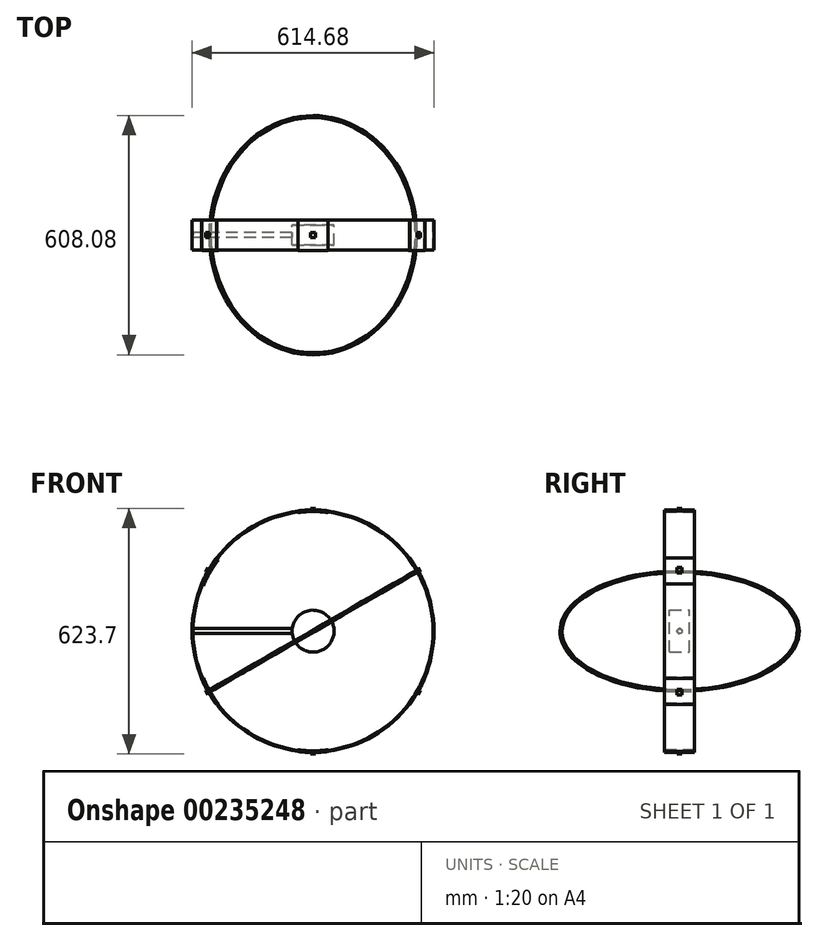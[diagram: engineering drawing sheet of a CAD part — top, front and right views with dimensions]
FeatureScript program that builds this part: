
annotation { "Feature Type Name" : "Feature", "Feature Type Description" : "" }
export const myFeature = defineFeature(function(context is Context, id is Id, definition is map)
    precondition{}
    {
        {
            var Q0;
            Q0=qCreatedBy(makeId("Front.planeOp"),FACE);
            var sketch = newSketch(context, id + "F0", { "sketchPlane" : qUnion([Q0])});
            skCircle(sketch, "E0", {"center": v(0, 0) * mm, "radius": 304.8 * mm});
            skCircle(sketch, "E1.0", {"center": v(0, 0) * mm, "radius": 307.34 * mm});
            skSolve(sketch);
        }
        {
            var Q0;
            Q0 = qSketchRegion(id + "F0", true);
            extrude(context, id + "F1", {"entities" : qUnion([Q0]), "endBound" : BoundingType.SYMMETRIC, "depth" : 76.2 * mm});
        }
        {
            var Q0;
            Q0=makeQuery(id+"F1.opExtrude","CAP_FACE",FACE,{"disambiguationData":[OSD([sQuery(id+"F0.wireOp",EDGE,"E0"),sQuery(id+"F0.wireOp",EDGE,"E1.0")])],"isStart":false});
            var sketch = newSketch(context, id + "F2", { "sketchPlane" : qUnion([Q0])});
            skLineSegment(sketch, "E2", {"start": v(0, 304.8) * mm, "end": v(0, 287.98) * mm, "construction": true});
            skArc(sketch, "E3.0", {"start": v(38.1, 304.97) * mm, "mid": v(0, 307.34) * mm, "end": v(-38.1, 304.97) * mm});
            skArc(sketch, "E4.0", {"start": v(38.1, 302.4) * mm, "mid": v(0, 304.8) * mm, "end": v(-38.1, 302.4) * mm});
            skLineSegment(sketch, "E5", {"start": v(-38.1, 302.4) * mm, "end": v(-38.1, 304.97) * mm, "construction": true});
            skLineSegment(sketch, "E6", {"start": v(38.1, 304.97) * mm, "end": v(38.1, 302.4) * mm, "construction": true});
            skArc(sketch, "E7.0", {"start": v(38.1, 301.64) * mm, "mid": v(0, 304.04) * mm, "end": v(-38.1, 301.64) * mm});
            skArc(sketch, "E8.0", {"start": v(38.1, 305.74) * mm, "mid": v(0, 308.1) * mm, "end": v(-38.1, 305.74) * mm});
            skLineSegment(sketch, "E9", {"start": v(-38.1, 302.4) * mm, "end": v(-38.1, 301.64) * mm});
            skLineSegment(sketch, "E10", {"start": v(-38.1, 304.97) * mm, "end": v(-38.1, 305.74) * mm});
            skLineSegment(sketch, "E11", {"start": v(38.1, 302.4) * mm, "end": v(38.1, 301.64) * mm});
            skLineSegment(sketch, "E12", {"start": v(38.1, 304.97) * mm, "end": v(38.1, 305.74) * mm});
            skArc(sketch, "E13.1.0", {"start": v(280.94, 118.2) * mm, "mid": v(263.96, 152.4) * mm, "end": v(242.84, 184.2) * mm});
            skArc(sketch, "E13.1.1", {"start": v(280.28, 117.83) * mm, "mid": v(263.3, 152.02) * mm, "end": v(242.18, 183.82) * mm});
            skArc(sketch, "E13.1.2", {"start": v(283.83, 119.87) * mm, "mid": v(266.82, 154.05) * mm, "end": v(245.73, 185.86) * mm});
            skArc(sketch, "E13.1.3", {"start": v(283.16, 119.49) * mm, "mid": v(266.16, 153.67) * mm, "end": v(245.06, 185.48) * mm});
            skLineSegment(sketch, "E13.1.4", {"start": v(242.84, 184.2) * mm, "end": v(245.06, 185.48) * mm, "construction": true});
            skLineSegment(sketch, "E13.1.5", {"start": v(283.16, 119.49) * mm, "end": v(280.94, 118.2) * mm, "construction": true});
            skLineSegment(sketch, "E13.1.6", {"start": v(242.84, 184.2) * mm, "end": v(242.18, 183.82) * mm});
            skLineSegment(sketch, "E13.1.7", {"start": v(245.06, 185.48) * mm, "end": v(245.73, 185.86) * mm});
            skLineSegment(sketch, "E13.1.8", {"start": v(280.94, 118.2) * mm, "end": v(280.28, 117.83) * mm});
            skLineSegment(sketch, "E13.1.9", {"start": v(283.16, 119.49) * mm, "end": v(283.83, 119.87) * mm});
            skArc(sketch, "E13.2.0", {"start": v(242.84, -184.2) * mm, "mid": v(263.96, -152.4) * mm, "end": v(280.94, -118.2) * mm});
            skArc(sketch, "E13.2.1", {"start": v(242.18, -183.82) * mm, "mid": v(263.3, -152.02) * mm, "end": v(280.28, -117.83) * mm});
            skArc(sketch, "E13.2.2", {"start": v(245.73, -185.86) * mm, "mid": v(266.82, -154.05) * mm, "end": v(283.83, -119.87) * mm});
            skArc(sketch, "E13.2.3", {"start": v(245.06, -185.48) * mm, "mid": v(266.16, -153.67) * mm, "end": v(283.16, -119.49) * mm});
            skLineSegment(sketch, "E13.2.4", {"start": v(280.94, -118.2) * mm, "end": v(283.16, -119.49) * mm, "construction": true});
            skLineSegment(sketch, "E13.2.5", {"start": v(245.06, -185.48) * mm, "end": v(242.84, -184.2) * mm, "construction": true});
            skLineSegment(sketch, "E13.2.6", {"start": v(280.94, -118.2) * mm, "end": v(280.28, -117.83) * mm});
            skLineSegment(sketch, "E13.2.7", {"start": v(283.16, -119.49) * mm, "end": v(283.83, -119.87) * mm});
            skLineSegment(sketch, "E13.2.8", {"start": v(242.84, -184.2) * mm, "end": v(242.18, -183.82) * mm});
            skLineSegment(sketch, "E13.2.9", {"start": v(245.06, -185.48) * mm, "end": v(245.73, -185.86) * mm});
            skArc(sketch, "E13.3.0", {"start": v(-38.1, -302.4) * mm, "mid": v(0, -304.8) * mm, "end": v(38.1, -302.4) * mm});
            skArc(sketch, "E13.3.1", {"start": v(-38.1, -301.64) * mm, "mid": v(0, -304.04) * mm, "end": v(38.1, -301.64) * mm});
            skArc(sketch, "E13.3.2", {"start": v(-38.1, -305.74) * mm, "mid": v(0, -308.1) * mm, "end": v(38.1, -305.74) * mm});
            skArc(sketch, "E13.3.3", {"start": v(-38.1, -304.97) * mm, "mid": v(0, -307.34) * mm, "end": v(38.1, -304.97) * mm});
            skLineSegment(sketch, "E13.3.4", {"start": v(38.1, -302.4) * mm, "end": v(38.1, -304.97) * mm, "construction": true});
            skLineSegment(sketch, "E13.3.5", {"start": v(-38.1, -304.97) * mm, "end": v(-38.1, -302.4) * mm, "construction": true});
            skLineSegment(sketch, "E13.3.6", {"start": v(38.1, -302.4) * mm, "end": v(38.1, -301.64) * mm});
            skLineSegment(sketch, "E13.3.7", {"start": v(38.1, -304.97) * mm, "end": v(38.1, -305.74) * mm});
            skLineSegment(sketch, "E13.3.8", {"start": v(-38.1, -302.4) * mm, "end": v(-38.1, -301.64) * mm});
            skLineSegment(sketch, "E13.3.9", {"start": v(-38.1, -304.97) * mm, "end": v(-38.1, -305.74) * mm});
            skArc(sketch, "E13.4.0", {"start": v(-280.94, -118.2) * mm, "mid": v(-263.96, -152.4) * mm, "end": v(-242.84, -184.2) * mm});
            skArc(sketch, "E13.4.1", {"start": v(-280.28, -117.83) * mm, "mid": v(-263.3, -152.02) * mm, "end": v(-242.18, -183.82) * mm});
            skArc(sketch, "E13.4.2", {"start": v(-283.83, -119.87) * mm, "mid": v(-266.82, -154.05) * mm, "end": v(-245.73, -185.86) * mm});
            skArc(sketch, "E13.4.3", {"start": v(-283.16, -119.49) * mm, "mid": v(-266.16, -153.67) * mm, "end": v(-245.06, -185.48) * mm});
            skLineSegment(sketch, "E13.4.4", {"start": v(-242.84, -184.2) * mm, "end": v(-245.06, -185.48) * mm, "construction": true});
            skLineSegment(sketch, "E13.4.5", {"start": v(-283.16, -119.49) * mm, "end": v(-280.94, -118.2) * mm, "construction": true});
            skLineSegment(sketch, "E13.4.6", {"start": v(-242.84, -184.2) * mm, "end": v(-242.18, -183.82) * mm});
            skLineSegment(sketch, "E13.4.7", {"start": v(-245.06, -185.48) * mm, "end": v(-245.73, -185.86) * mm});
            skLineSegment(sketch, "E13.4.8", {"start": v(-280.94, -118.2) * mm, "end": v(-280.28, -117.83) * mm});
            skLineSegment(sketch, "E13.4.9", {"start": v(-283.16, -119.49) * mm, "end": v(-283.83, -119.87) * mm});
            skArc(sketch, "E13.5.0", {"start": v(-242.84, 184.2) * mm, "mid": v(-263.96, 152.4) * mm, "end": v(-280.94, 118.2) * mm});
            skArc(sketch, "E13.5.1", {"start": v(-242.18, 183.82) * mm, "mid": v(-263.3, 152.02) * mm, "end": v(-280.28, 117.83) * mm});
            skArc(sketch, "E13.5.2", {"start": v(-245.73, 185.86) * mm, "mid": v(-266.82, 154.05) * mm, "end": v(-283.83, 119.87) * mm});
            skArc(sketch, "E13.5.3", {"start": v(-245.06, 185.48) * mm, "mid": v(-266.16, 153.67) * mm, "end": v(-283.16, 119.49) * mm});
            skLineSegment(sketch, "E13.5.4", {"start": v(-280.94, 118.2) * mm, "end": v(-283.16, 119.49) * mm, "construction": true});
            skLineSegment(sketch, "E13.5.5", {"start": v(-245.06, 185.48) * mm, "end": v(-242.84, 184.2) * mm, "construction": true});
            skLineSegment(sketch, "E13.5.6", {"start": v(-280.94, 118.2) * mm, "end": v(-280.28, 117.83) * mm});
            skLineSegment(sketch, "E13.5.7", {"start": v(-283.16, 119.49) * mm, "end": v(-283.83, 119.87) * mm});
            skLineSegment(sketch, "E13.5.8", {"start": v(-242.84, 184.2) * mm, "end": v(-242.18, 183.82) * mm});
            skLineSegment(sketch, "E13.5.9", {"start": v(-245.06, 185.48) * mm, "end": v(-245.73, 185.86) * mm});
            skLineSegment(sketch, "E13.anchor1", {"start": v(0, 0) * mm, "end": v(-38.1, 301.64) * mm, "construction": true});
            skLineSegment(sketch, "E13.anchor2", {"start": v(0, 0) * mm, "end": v(-38.1, 301.64) * mm, "construction": true});
            skSolve(sketch);
        }
        {
            var Q0;
            Q0 = qSketchRegion(id + "F2", true);
            var Q1;
            Q1=makeQuery(id+"F1.opExtrude","CAP_FACE",FACE,{"disambiguationData":[OSD([sQuery(id+"F0.wireOp",EDGE,"E0"),sQuery(id+"F0.wireOp",EDGE,"E1.0")])],"isStart":true});
            extrude(context, id + "F3", {"entities" : qUnion([Q0]), "operationType" : NewBodyOperationType.ADD, "endBound" : BoundingType.UP_TO_SURFACE, "oppositeDirection" : true, "endBoundEntityFace" : qUnion([Q1]), "depth" : 162.56 * mm});
        }
        {
            var Q0;
            Q0=makeQuery(id+"F3.boolean.opBoolean","MERGE",FACE,{"derivedFrom":[makeQuery(id+"F1.opExtrude","CAP_FACE",FACE,{"disambiguationData":[OSD([sQuery(id+"F0.wireOp",EDGE,"E0"),sQuery(id+"F0.wireOp",EDGE,"E1.0")])],"isStart":false}),makeQuery(id+"F3.opExtrude","CAP_FACE",FACE,{"disambiguationData":[OSD([sQuery(id+"F2.wireOp",EDGE,"E13.1.0"),sQuery(id+"F2.wireOp",EDGE,"E13.1.1"),sQuery(id+"F2.wireOp",EDGE,"E13.1.6"),sQuery(id+"F2.wireOp",EDGE,"E13.1.8")])],"isStart":true}),makeQuery(id+"F3.opExtrude","CAP_FACE",FACE,{"disambiguationData":[OSD([sQuery(id+"F2.wireOp",EDGE,"E13.1.2"),sQuery(id+"F2.wireOp",EDGE,"E13.1.3"),sQuery(id+"F2.wireOp",EDGE,"E13.1.7"),sQuery(id+"F2.wireOp",EDGE,"E13.1.9")])],"isStart":true}),makeQuery(id+"F3.opExtrude","CAP_FACE",FACE,{"disambiguationData":[OSD([sQuery(id+"F2.wireOp",EDGE,"E13.2.0"),sQuery(id+"F2.wireOp",EDGE,"E13.2.1"),sQuery(id+"F2.wireOp",EDGE,"E13.2.6"),sQuery(id+"F2.wireOp",EDGE,"E13.2.8")])],"isStart":true}),makeQuery(id+"F3.opExtrude","CAP_FACE",FACE,{"disambiguationData":[OSD([sQuery(id+"F2.wireOp",EDGE,"E13.2.2"),sQuery(id+"F2.wireOp",EDGE,"E13.2.3"),sQuery(id+"F2.wireOp",EDGE,"E13.2.7"),sQuery(id+"F2.wireOp",EDGE,"E13.2.9")])],"isStart":true}),makeQuery(id+"F3.opExtrude","CAP_FACE",FACE,{"disambiguationData":[OSD([sQuery(id+"F2.wireOp",EDGE,"E13.3.0"),sQuery(id+"F2.wireOp",EDGE,"E13.3.1"),sQuery(id+"F2.wireOp",EDGE,"E13.3.6"),sQuery(id+"F2.wireOp",EDGE,"E13.3.8")])],"isStart":true}),makeQuery(id+"F3.opExtrude","CAP_FACE",FACE,{"disambiguationData":[OSD([sQuery(id+"F2.wireOp",EDGE,"E13.3.2"),sQuery(id+"F2.wireOp",EDGE,"E13.3.3"),sQuery(id+"F2.wireOp",EDGE,"E13.3.7"),sQuery(id+"F2.wireOp",EDGE,"E13.3.9")])],"isStart":true}),makeQuery(id+"F3.opExtrude","CAP_FACE",FACE,{"disambiguationData":[OSD([sQuery(id+"F2.wireOp",EDGE,"E13.4.0"),sQuery(id+"F2.wireOp",EDGE,"E13.4.1"),sQuery(id+"F2.wireOp",EDGE,"E13.4.6"),sQuery(id+"F2.wireOp",EDGE,"E13.4.8")])],"isStart":true}),makeQuery(id+"F3.opExtrude","CAP_FACE",FACE,{"disambiguationData":[OSD([sQuery(id+"F2.wireOp",EDGE,"E13.4.2"),sQuery(id+"F2.wireOp",EDGE,"E13.4.3"),sQuery(id+"F2.wireOp",EDGE,"E13.4.7"),sQuery(id+"F2.wireOp",EDGE,"E13.4.9")])],"isStart":true}),makeQuery(id+"F3.opExtrude","CAP_FACE",FACE,{"disambiguationData":[OSD([sQuery(id+"F2.wireOp",EDGE,"E13.5.0"),sQuery(id+"F2.wireOp",EDGE,"E13.5.1"),sQuery(id+"F2.wireOp",EDGE,"E13.5.6"),sQuery(id+"F2.wireOp",EDGE,"E13.5.8")])],"isStart":true}),makeQuery(id+"F3.opExtrude","CAP_FACE",FACE,{"disambiguationData":[OSD([sQuery(id+"F2.wireOp",EDGE,"E13.5.2"),sQuery(id+"F2.wireOp",EDGE,"E13.5.3"),sQuery(id+"F2.wireOp",EDGE,"E13.5.7"),sQuery(id+"F2.wireOp",EDGE,"E13.5.9")])],"isStart":true}),makeQuery(id+"F3.opExtrude","CAP_FACE",FACE,{"disambiguationData":[OSD([sQuery(id+"F2.wireOp",EDGE,"E4.0"),sQuery(id+"F2.wireOp",EDGE,"E7.0"),sQuery(id+"F2.wireOp",EDGE,"E9"),sQuery(id+"F2.wireOp",EDGE,"E11")])],"isStart":true}),makeQuery(id+"F3.opExtrude","CAP_FACE",FACE,{"disambiguationData":[OSD([sQuery(id+"F2.wireOp",EDGE,"E8.0"),sQuery(id+"F2.wireOp",EDGE,"E3.0"),sQuery(id+"F2.wireOp",EDGE,"E10"),sQuery(id+"F2.wireOp",EDGE,"E12")])],"isStart":true})]});
            var sketch = newSketch(context, id + "F4", { "sketchPlane" : qUnion([Q0])});
            skArc(sketch, "E14.0", {"start": v(38.1, 305.74) * mm, "mid": v(0, 308.1) * mm, "end": v(-38.1, 305.74) * mm});
            skArc(sketch, "E14.1", {"start": v(38.1, 301.64) * mm, "mid": v(0, 304.04) * mm, "end": v(-38.1, 301.64) * mm});
            skLineSegment(sketch, "E15", {"start": v(38.1, 301.64) * mm, "end": v(38.1, 305.74) * mm});
            skLineSegment(sketch, "E16", {"start": v(-38.1, 305.74) * mm, "end": v(-38.1, 301.64) * mm});
            skArc(sketch, "E17.1.0", {"start": v(280.28, 117.83) * mm, "mid": v(263.3, 152.02) * mm, "end": v(242.18, 183.82) * mm});
            skArc(sketch, "E17.1.1", {"start": v(283.83, 119.87) * mm, "mid": v(266.82, 154.05) * mm, "end": v(245.73, 185.86) * mm});
            skLineSegment(sketch, "E17.1.2", {"start": v(280.28, 117.83) * mm, "end": v(283.83, 119.87) * mm});
            skLineSegment(sketch, "E17.1.3", {"start": v(245.73, 185.86) * mm, "end": v(242.18, 183.82) * mm});
            skArc(sketch, "E17.2.0", {"start": v(242.18, -183.82) * mm, "mid": v(263.3, -152.02) * mm, "end": v(280.28, -117.83) * mm});
            skArc(sketch, "E17.2.1", {"start": v(245.73, -185.86) * mm, "mid": v(266.82, -154.05) * mm, "end": v(283.83, -119.87) * mm});
            skLineSegment(sketch, "E17.2.2", {"start": v(242.18, -183.82) * mm, "end": v(245.73, -185.86) * mm});
            skLineSegment(sketch, "E17.2.3", {"start": v(283.83, -119.87) * mm, "end": v(280.28, -117.83) * mm});
            skArc(sketch, "E17.3.0", {"start": v(-38.1, -301.64) * mm, "mid": v(0, -304.04) * mm, "end": v(38.1, -301.64) * mm});
            skArc(sketch, "E17.3.1", {"start": v(-38.1, -305.74) * mm, "mid": v(0, -308.1) * mm, "end": v(38.1, -305.74) * mm});
            skLineSegment(sketch, "E17.3.2", {"start": v(-38.1, -301.64) * mm, "end": v(-38.1, -305.74) * mm});
            skLineSegment(sketch, "E17.3.3", {"start": v(38.1, -305.74) * mm, "end": v(38.1, -301.64) * mm});
            skLineSegment(sketch, "E17.anchor1", {"start": v(0, 0) * mm, "end": v(-38.1, 301.64) * mm, "construction": true});
            skLineSegment(sketch, "E17.anchor2", {"start": v(0, 0) * mm, "end": v(38.1, -301.64) * mm, "construction": true});
            skArc(sketch, "E18.1.0", {"start": v(-278.73, -118.72) * mm, "mid": v(-261.75, -152.91) * mm, "end": v(-240.63, -184.71) * mm});
            skArc(sketch, "E18.1.1", {"start": v(-282.27, -120.77) * mm, "mid": v(-265.27, -154.95) * mm, "end": v(-244.17, -186.76) * mm});
            skLineSegment(sketch, "E18.1.2", {"start": v(-278.73, -118.72) * mm, "end": v(-282.27, -120.77) * mm});
            skLineSegment(sketch, "E18.1.3", {"start": v(-244.17, -186.76) * mm, "end": v(-240.63, -184.71) * mm});
            skArc(sketch, "E18.2.0", {"start": v(-240.63, 181.13) * mm, "mid": v(-261.75, 149.33) * mm, "end": v(-278.73, 115.14) * mm});
            skArc(sketch, "E18.2.1", {"start": v(-244.17, 183.18) * mm, "mid": v(-265.27, 151.36) * mm, "end": v(-282.27, 117.19) * mm});
            skLineSegment(sketch, "E18.2.2", {"start": v(-240.63, 181.13) * mm, "end": v(-244.17, 183.18) * mm});
            skLineSegment(sketch, "E18.2.3", {"start": v(-282.27, 117.19) * mm, "end": v(-278.73, 115.14) * mm});
            skPoint(sketch, "E18.center", {"position": v(0, -1.8) * mm});
            skLineSegment(sketch, "E18.anchor1", {"start": v(0, -1.8) * mm, "end": v(-38.1, -305.74) * mm, "construction": true});
            skLineSegment(sketch, "E18.anchor2", {"start": v(0, -1.8) * mm, "end": v(-244.17, 183.18) * mm, "construction": true});
            skSolve(sketch);
        }
        {
            var Q0;
            Q0 = qSketchRegion(id + "F4", true);
            extrude(context, id + "F5", {"entities" : qUnion([Q0]), "operationType" : NewBodyOperationType.ADD, "depth" : 0.76 * mm});
        }
        {
            var Q0;
            Q0=qCreatedBy(makeId("Front.planeOp"),FACE);
            var sketch = newSketch(context, id + "F6", { "sketchPlane" : qUnion([Q0])});
            skLineSegment(sketch, "E19", {"start": v(0, 0) * mm, "end": v(0, 308.1) * mm, "construction": true});
            skArc(sketch, "E20.0", {"start": v(6.35, 308.04) * mm, "mid": v(0, 308.1) * mm, "end": v(-6.35, 308.04) * mm});
            skLineSegment(sketch, "E21", {"start": v(-6.35, 308.04) * mm, "end": v(-6.35, 311.85) * mm});
            skLineSegment(sketch, "E22", {"start": v(-6.35, 311.85) * mm, "end": v(6.35, 311.85) * mm});
            skLineSegment(sketch, "E23", {"start": v(6.35, 311.85) * mm, "end": v(6.35, 308.04) * mm});
            skPoint(sketch, "E24.orphan", {"position": v(-38.1, 305.74) * mm});
            skPoint(sketch, "E25.orphan", {"position": v(38.1, 305.74) * mm});
            skArc(sketch, "E26.1.0", {"start": v(269.94, 148.52) * mm, "mid": v(266.82, 154.05) * mm, "end": v(263.6, 159.52) * mm});
            skLineSegment(sketch, "E26.1.1", {"start": v(263.6, 159.52) * mm, "end": v(266.9, 161.42) * mm});
            skLineSegment(sketch, "E26.1.2", {"start": v(273.24, 150.42) * mm, "end": v(269.94, 148.52) * mm});
            skLineSegment(sketch, "E26.1.3", {"start": v(266.9, 161.42) * mm, "end": v(273.24, 150.42) * mm});
            skArc(sketch, "E26.2.0", {"start": v(263.6, -159.52) * mm, "mid": v(266.82, -154.05) * mm, "end": v(269.94, -148.52) * mm});
            skLineSegment(sketch, "E26.2.1", {"start": v(269.94, -148.52) * mm, "end": v(273.24, -150.42) * mm});
            skLineSegment(sketch, "E26.2.2", {"start": v(266.9, -161.42) * mm, "end": v(263.6, -159.52) * mm});
            skLineSegment(sketch, "E26.2.3", {"start": v(273.24, -150.42) * mm, "end": v(266.9, -161.42) * mm});
            skArc(sketch, "E26.3.0", {"start": v(-6.35, -308.04) * mm, "mid": v(0, -308.1) * mm, "end": v(6.35, -308.04) * mm});
            skLineSegment(sketch, "E26.3.1", {"start": v(6.35, -308.04) * mm, "end": v(6.35, -311.85) * mm});
            skLineSegment(sketch, "E26.3.2", {"start": v(-6.35, -311.85) * mm, "end": v(-6.35, -308.04) * mm});
            skLineSegment(sketch, "E26.3.3", {"start": v(6.35, -311.85) * mm, "end": v(-6.35, -311.85) * mm});
            skArc(sketch, "E26.4.0", {"start": v(-269.94, -148.52) * mm, "mid": v(-266.82, -154.05) * mm, "end": v(-263.6, -159.52) * mm});
            skLineSegment(sketch, "E26.4.1", {"start": v(-263.6, -159.52) * mm, "end": v(-266.9, -161.42) * mm});
            skLineSegment(sketch, "E26.4.2", {"start": v(-273.24, -150.42) * mm, "end": v(-269.94, -148.52) * mm});
            skLineSegment(sketch, "E26.4.3", {"start": v(-266.9, -161.42) * mm, "end": v(-273.24, -150.42) * mm});
            skArc(sketch, "E26.5.0", {"start": v(-263.6, 159.52) * mm, "mid": v(-266.82, 154.05) * mm, "end": v(-269.94, 148.52) * mm});
            skLineSegment(sketch, "E26.5.1", {"start": v(-269.94, 148.52) * mm, "end": v(-273.24, 150.42) * mm});
            skLineSegment(sketch, "E26.5.2", {"start": v(-266.9, 161.42) * mm, "end": v(-263.6, 159.52) * mm});
            skLineSegment(sketch, "E26.5.3", {"start": v(-273.24, 150.42) * mm, "end": v(-266.9, 161.42) * mm});
            skLineSegment(sketch, "E26.anchor1", {"start": v(0, 0) * mm, "end": v(-6.35, 308.04) * mm, "construction": true});
            skSolve(sketch);
        }
        {
            var Q0;
            Q0 = qSketchRegion(id + "F6", true);
            extrude(context, id + "F7", {"entities" : qUnion([Q0]), "operationType" : NewBodyOperationType.ADD, "endBound" : BoundingType.SYMMETRIC, "depth" : 12.7 * mm});
        }
        {
            var Q0;
            Q0=qCreatedBy(makeId("Front.planeOp"),FACE);
            var sketch = newSketch(context, id + "F8", { "sketchPlane" : qUnion([Q0])});
            skLineSegment(sketch, "E27", {"start": v(0, 0) * mm, "end": v(263.3, 152.02) * mm, "construction": true});
            skCircle(sketch, "E28", {"center": v(261.1, 150.75) * mm, "radius": 2.54 * mm});
            skLineSegment(sketch, "E29", {"start": v(0, 0) * mm, "end": v(-122.52, 212.2) * mm, "construction": true});
            skSolve(sketch);
        }
        {
            var Q0;
            Q0 = qSketchRegion(id + "F8", true);
            var Q1;
            Q1=sQuery(id+"F8.wireOp",EDGE,"E29");
            revolve(context, id + "F9", {"entities" : qUnion([Q0]), "axis" : qUnion([Q1]), "revolveType" : RevolveType.FULL});
        }
        {
            var Q0;
            Q0=qCreatedBy(makeId("Front.planeOp"),FACE);
            var sketch = newSketch(context, id + "F10", { "sketchPlane" : qUnion([Q0])});
            skArc(sketch, "E30.0", {"start": v(-280.94, 118.2) * mm, "mid": v(-304.8, 0) * mm, "end": v(-280.94, -118.2) * mm});
            skLineSegment(sketch, "E31", {"start": v(-304.8, 0) * mm, "end": v(0, 0) * mm, "construction": true});
            skLineSegment(sketch, "E32.0", {"start": v(-304.73, -6.35) * mm, "end": v(0, -6.35) * mm});
            skLineSegment(sketch, "E33.0", {"start": v(-304.73, 6.35) * mm, "end": v(0, 6.35) * mm});
            skLineSegment(sketch, "E34", {"start": v(0, -6.35) * mm, "end": v(0, 6.35) * mm});
            skSolve(sketch);
        }
        {
            var Q0;
            {var subQ0=sQuery(id+"F10.wireOp",EDGE,"E32.0");Q0=makeQuery(id+"F10.imprint","IMPRINT",FACE,{"disambiguationData":[TD([[makeQuery(id+"F10.imprint","IMPRINT",EDGE,{"derivedFrom":subQ0}),1.0]])]});}
            extrude(context, id + "F11", {"entities" : qUnion([Q0]), "endBound" : BoundingType.SYMMETRIC, "depth" : 12.7 * mm});
        }
        {
            var Q0;
            Q0=makeQuery(id+"F11.opExtrude","CAP_EDGE",EDGE,{"disambiguationData":[OSD([sQuery(id+"F10.wireOp",EDGE,"E33.0")])],"isStart":true});
            var Q1;
            Q1=makeQuery(id+"F11.opExtrude","CAP_EDGE",EDGE,{"disambiguationData":[OSD([sQuery(id+"F10.wireOp",EDGE,"E33.0")])],"isStart":false});
            var Q2;
            Q2=makeQuery(id+"F11.opExtrude","CAP_EDGE",EDGE,{"disambiguationData":[OSD([sQuery(id+"F10.wireOp",EDGE,"E32.0")])],"isStart":true});
            var Q3;
            Q3=makeQuery(id+"F11.opExtrude","CAP_EDGE",EDGE,{"disambiguationData":[OSD([sQuery(id+"F10.wireOp",EDGE,"E32.0")])],"isStart":false});
            fillet(context, id + "F12", {"entities" : qUnion([Q0, Q1, Q2, Q3]), "radius" : 6.35 * mm, "tangentPropagation" : true, "allowEdgeOverflow" : false});
        }
        {
            var Q0;
            Q0=makeQuery(id+"F11.opExtrude","SWEPT_FACE",FACE,{"disambiguationData":[OSD([sQuery(id+"F10.wireOp",EDGE,"E34")])]});
            var sketch = newSketch(context, id + "F13", { "sketchPlane" : qUnion([Q0])});
            skCircle(sketch, "E35.0", {"center": v(0, 0) * mm, "radius": 6.35 * mm});
            skSolve(sketch);
        }
        {
            var Q0;
            Q0 = qSketchRegion(id + "F13", true);
            extrude(context, id + "F14", {"entities" : qUnion([Q0]), "operationType" : NewBodyOperationType.REMOVE, "oppositeDirection" : true, "depth" : 53.34 * mm});
        }
        {
            var Q0;
            Q0=qCreatedBy(makeId("Front.planeOp"),FACE);
            var sketch = newSketch(context, id + "F15", { "sketchPlane" : qUnion([Q0])});
            skCircle(sketch, "E36", {"center": v(0, 0) * mm, "radius": 53.34 * mm});
            skSolve(sketch);
        }
        {
            var Q0;
            Q0 = qSketchRegion(id + "F15", true);
            extrude(context, id + "F16", {"entities" : qUnion([Q0]), "operationType" : NewBodyOperationType.ADD, "endBound" : BoundingType.SYMMETRIC, "depth" : 50.8 * mm});
        }
    });
